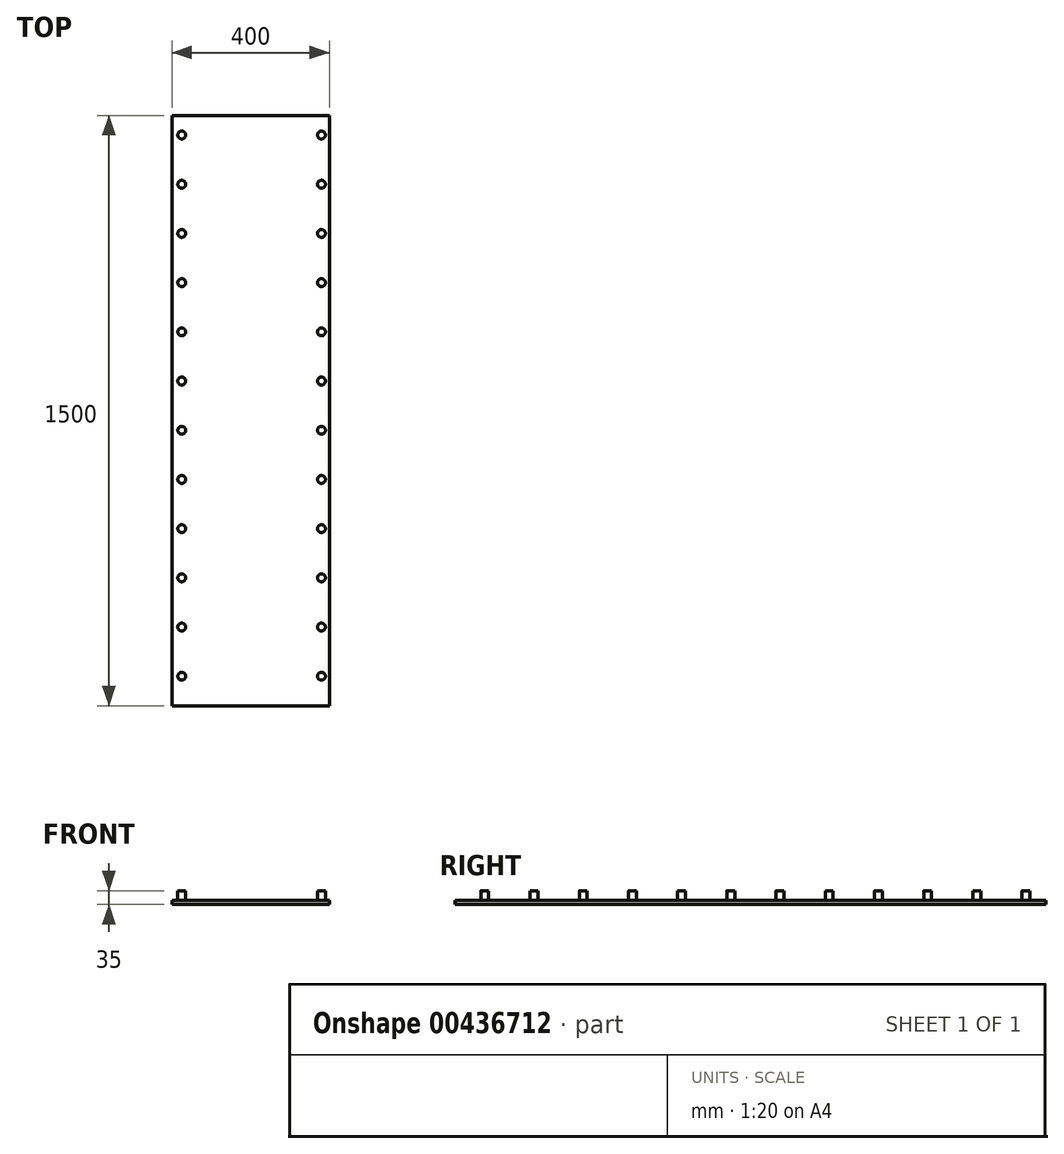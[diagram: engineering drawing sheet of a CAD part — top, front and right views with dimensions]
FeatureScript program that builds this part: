
annotation { "Feature Type Name" : "Feature", "Feature Type Description" : "" }
export const myFeature = defineFeature(function(context is Context, id is Id, definition is map)
    precondition{}
    {
        {
            var Q0;
            Q0=qCreatedBy(makeId("Top.planeOp"),FACE);
            var sketch = newSketch(context, id + "F0", { "sketchPlane" : qUnion([Q0])});
            skCircle(sketch, "E0", {"center": v(0, 0) * mm, "radius": 10 * mm});
            skCircle(sketch, "E1.0.1.0", {"center": v(0, 125) * mm, "radius": 10 * mm});
            skCircle(sketch, "E1.0.2.0", {"center": v(0, 250) * mm, "radius": 10 * mm});
            skCircle(sketch, "E1.0.3.0", {"center": v(0, 375) * mm, "radius": 10 * mm});
            skCircle(sketch, "E1.0.4.0", {"center": v(0, 500) * mm, "radius": 10 * mm});
            skCircle(sketch, "E1.0.5.0", {"center": v(0, 625) * mm, "radius": 10 * mm});
            skCircle(sketch, "E1.0.6.0", {"center": v(0, 750) * mm, "radius": 10 * mm});
            skCircle(sketch, "E1.0.7.0", {"center": v(0, 875) * mm, "radius": 10 * mm});
            skCircle(sketch, "E1.0.8.0", {"center": v(0, 1000) * mm, "radius": 10 * mm});
            skCircle(sketch, "E1.0.9.0", {"center": v(0, 1125) * mm, "radius": 10 * mm});
            skCircle(sketch, "E1.0.10.0", {"center": v(0, 1250) * mm, "radius": 10 * mm});
            skCircle(sketch, "E1.0.11.0", {"center": v(0, 1375) * mm, "radius": 10 * mm});
            skCircle(sketch, "E1.1.0.0", {"center": v(355, 0) * mm, "radius": 10 * mm});
            skCircle(sketch, "E1.1.1.0", {"center": v(355, 125) * mm, "radius": 10 * mm});
            skCircle(sketch, "E1.1.2.0", {"center": v(355, 250) * mm, "radius": 10 * mm});
            skCircle(sketch, "E1.1.3.0", {"center": v(355, 375) * mm, "radius": 10 * mm});
            skCircle(sketch, "E1.1.4.0", {"center": v(355, 500) * mm, "radius": 10 * mm});
            skCircle(sketch, "E1.1.5.0", {"center": v(355, 625) * mm, "radius": 10 * mm});
            skCircle(sketch, "E1.1.6.0", {"center": v(355, 750) * mm, "radius": 10 * mm});
            skCircle(sketch, "E1.1.7.0", {"center": v(355, 875) * mm, "radius": 10 * mm});
            skCircle(sketch, "E1.1.8.0", {"center": v(355, 1000) * mm, "radius": 10 * mm});
            skCircle(sketch, "E1.1.9.0", {"center": v(355, 1125) * mm, "radius": 10 * mm});
            skCircle(sketch, "E1.1.10.0", {"center": v(355, 1250) * mm, "radius": 10 * mm});
            skCircle(sketch, "E1.1.11.0", {"center": v(355, 1375) * mm, "radius": 10 * mm});
            skLineSegment(sketch, "E1.direction1", {"start": v(0, 0) * mm, "end": v(355, 0) * mm, "construction": true});
            skLineSegment(sketch, "E1.direction2", {"start": v(0, 0) * mm, "end": v(0, 125) * mm, "construction": true});
            skSolve(sketch);
        }
        {
            var Q0;
            Q0=qCreatedBy(makeId("Top.planeOp"),FACE);
            var sketch = newSketch(context, id + "F1", { "sketchPlane" : qUnion([Q0])});
            skLineSegment(sketch, "E2.bottom", {"start": v(-25, 1425) * mm, "end": v(375, 1425) * mm});
            skLineSegment(sketch, "E2.top", {"start": v(-25, -75) * mm, "end": v(375, -75) * mm});
            skLineSegment(sketch, "E2.left", {"start": v(-25, 1425) * mm, "end": v(-25, -75) * mm});
            skLineSegment(sketch, "E2.right", {"start": v(375, 1425) * mm, "end": v(375, -75) * mm});
            skSolve(sketch);
        }
        {
            var Q0;
            Q0=makeQuery(id+"F1.imprint","IMPRINT",FACE,{"disambiguationData":[TD([[makeQuery(id+"F1.imprint","IMPRINT",EDGE,{"derivedFrom":sQuery(id+"F1.wireOp",EDGE,"E2.bottom")}),-1.0]])]});
            extrude(context, id + "F2", {"entities" : qUnion([Q0]), "oppositeDirection" : true, "depth" : 10 * mm});
        }
        {
            var Q0;
            Q0 = qSketchRegion(id + "F0", true);
            extrude(context, id + "F3", {"entities" : qUnion([Q0]), "operationType" : NewBodyOperationType.ADD, "depth" : 25 * mm});
        }
    });
